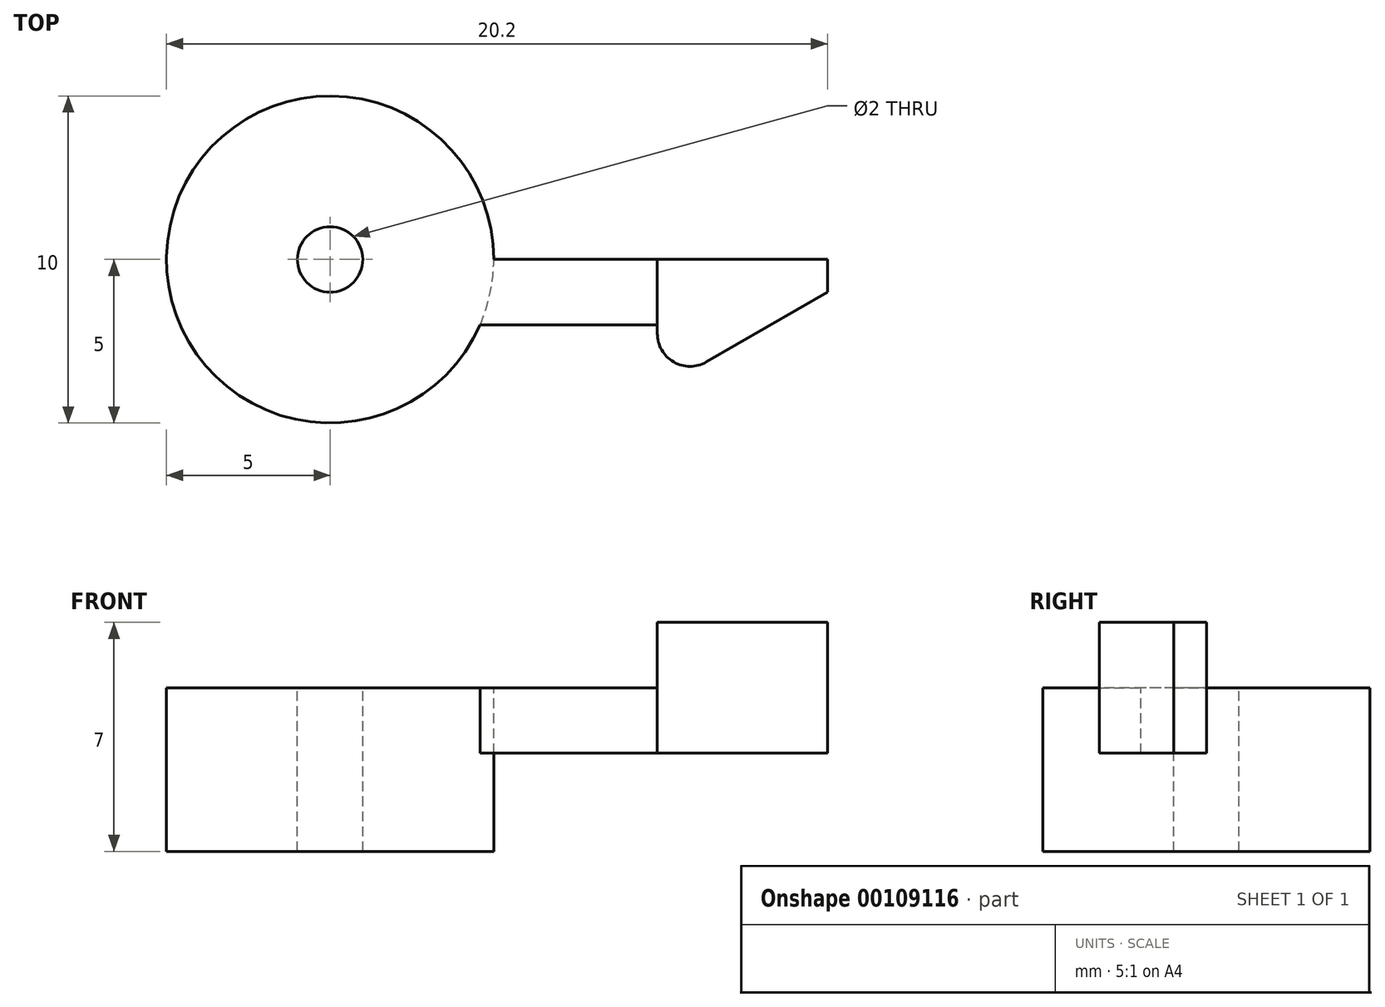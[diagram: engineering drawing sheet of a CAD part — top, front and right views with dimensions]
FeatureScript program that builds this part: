
annotation { "Feature Type Name" : "Feature", "Feature Type Description" : "" }
export const myFeature = defineFeature(function(context is Context, id is Id, definition is map)
    precondition{}
    {
        {
            var Q0;
            Q0=qCreatedBy(makeId("Top.planeOp"),FACE);
            var sketch = newSketch(context, id + "F0", { "sketchPlane" : qUnion([Q0])});
            skCircle(sketch, "E0", {"center": v(0, 0) * mm, "radius": 5 * mm});
            skLineSegment(sketch, "E1", {"start": v(5, 0) * mm, "end": v(10, 0) * mm});
            skLineSegment(sketch, "E2", {"start": v(10, 0) * mm, "end": v(15.2, 0) * mm});
            skLineSegment(sketch, "E3.MirrorCS", {"start": v(10, -2) * mm, "end": v(4.58, -2) * mm});
            skLineSegment(sketch, "E4.MirrorCS", {"start": v(15.2, -1) * mm, "end": v(10, -4) * mm});
            skLineSegment(sketch, "E5.MirrorCS", {"start": v(10, 0) * mm, "end": v(10, -2) * mm});
            skLineSegment(sketch, "E6.MirrorCS", {"start": v(10, -4) * mm, "end": v(10, -2) * mm});
            skLineSegment(sketch, "E7.MirrorCS", {"start": v(15.2, 0) * mm, "end": v(15.2, -1) * mm});
            skSolve(sketch);
        }
        {
            var Q0;
            {var subQ0=sQuery(id+"F0.wireOp",EDGE,"E0");var subQ1=makeQuery(id+"F0.imprint","INTERSECT",VERTEX,{"derivedFrom":[subQ0,sQuery(id+"F0.wireOp",EDGE,"E1")]});Q0=makeQuery(id+"F0.imprint","IMPRINT",FACE,{"disambiguationData":[TD([[makeQuery(id+"F0.imprint","IMPRINT",EDGE,{"disambiguationData":[TD([[subQ1,-1.0]])],"derivedFrom":subQ0}),1.0]])]});}
            extrude(context, id + "F1", {"entities" : qUnion([Q0]), "oppositeDirection" : true, "depth" : 5 * mm});
        }
        {
            var Q0;
            {var subQ0=sQuery(id+"F0.wireOp",EDGE,"E1");Q0=makeQuery(id+"F0.imprint","IMPRINT",FACE,{"disambiguationData":[TD([[makeQuery(id+"F0.imprint","IMPRINT",EDGE,{"derivedFrom":subQ0}),-1.0]])]});}
            extrude(context, id + "F2", {"entities" : qUnion([Q0]), "operationType" : NewBodyOperationType.ADD, "oppositeDirection" : true, "depth" : 2 * mm});
        }
        {
            var Q0;
            Q0=makeQuery(id+"F0.imprint","IMPRINT",FACE,{"disambiguationData":[TD([[makeQuery(id+"F0.imprint","IMPRINT",EDGE,{"derivedFrom":sQuery(id+"F0.wireOp",EDGE,"E2")}),-1.0]])]});
            extrude(context, id + "F3", {"entities" : qUnion([Q0]), "operationType" : NewBodyOperationType.ADD, "endBound" : BoundingType.SYMMETRIC, "depth" : 4 * mm});
        }
        {
            var Q0;
            Q0=sQuery(id+"F0.wireOp",VERTEX,"E0.center");
            var Q1;
            Q1=makeQuery(id+"F1.opExtrude","SWEPT_BODY",BODY,{"disambiguationData":[OSD([sQuery(id+"F0.wireOp",EDGE,"E0")])]});
            hole(context, id + "F4", {"style" : HoleStyle.SIMPLE, "endStyle" : HoleEndStyle.THROUGH, "holeDiameter" : 2 * mm, "locations" : qUnion([Q0]), "scope" : qUnion([Q1]), "isTappedThrough" : true});
        }
        {
            var Q0;
            Q0=makeQuery(id+"F3.opExtrude","SWEPT_EDGE",EDGE,{"disambiguationData":[OSD([sQuery(id+"F0.wireOp",EDGE,"E6.MirrorCS"),sQuery(id+"F0.wireOp",EDGE,"E4.MirrorCS")])]});
            fillet(context, id + "F5", {"entities" : qUnion([Q0]), "radius" : 1 * mm, "tangentPropagation" : true, "allowEdgeOverflow" : false});
        }
    });
